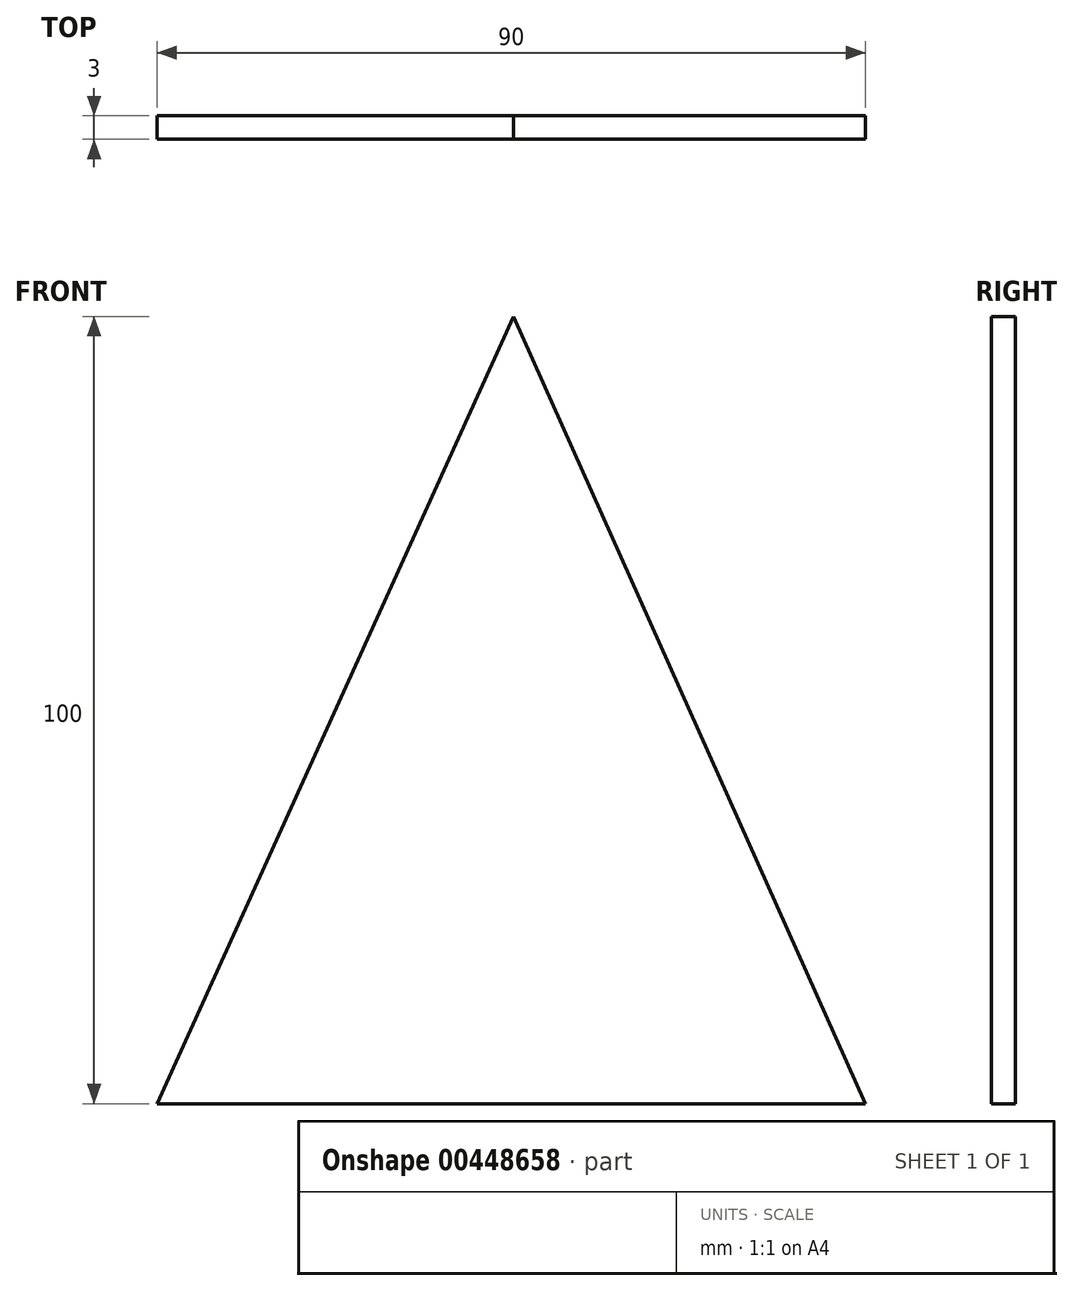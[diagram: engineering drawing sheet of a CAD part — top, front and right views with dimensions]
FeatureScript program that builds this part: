
annotation { "Feature Type Name" : "Feature", "Feature Type Description" : "" }
export const myFeature = defineFeature(function(context is Context, id is Id, definition is map)
    precondition{}
    {
        {
            var Q0;
            Q0=qCreatedBy(makeId("Front.planeOp"),FACE);
            var sketch = newSketch(context, id + "F0", { "sketchPlane" : qUnion([Q0])});
            skLineSegment(sketch, "E0", {"start": v(-45.25, 0) * mm, "end": v(44.75, 0) * mm});
            skLineSegment(sketch, "E1", {"start": v(44.75, 0) * mm, "end": v(0, 100) * mm});
            skLineSegment(sketch, "E2", {"start": v(0, 100) * mm, "end": v(-45.25, 0) * mm});
            skLineSegment(sketch, "E3.MirrorCS", {"start": v(0, 100) * mm, "end": v(45.25, 0) * mm});
            skLineSegment(sketch, "E4", {"start": v(0, 100) * mm, "end": v(0, 0) * mm, "construction": true});
            skSolve(sketch);
        }
        {
            var Q0;
            Q0 = qSketchRegion(id + "F0", true);
            extrude(context, id + "F1", {"entities" : qUnion([Q0]), "depth" : 3 * mm});
        }
    });
